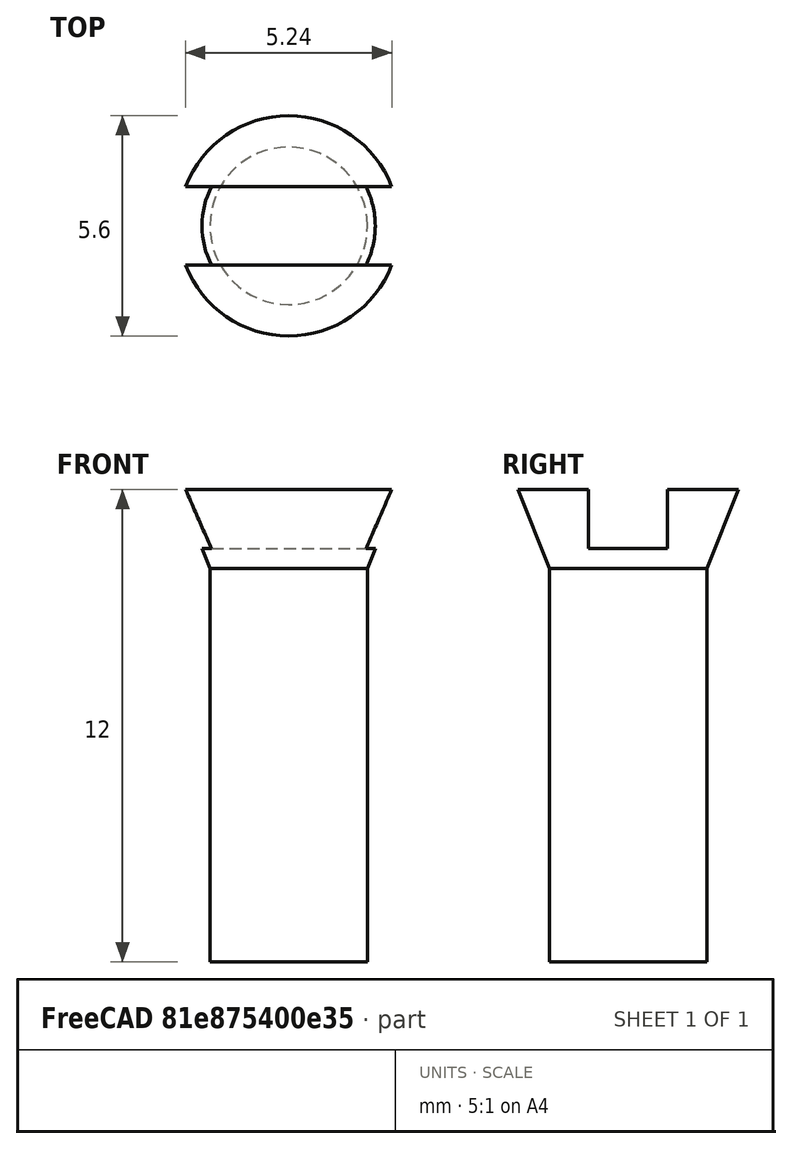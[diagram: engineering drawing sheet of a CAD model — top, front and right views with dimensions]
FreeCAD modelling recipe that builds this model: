
FCSTD DOCUMENT  (FreeCAD 0.21R33694 (Git))
Label: OJT1_T014R013_cargol
License: All rights reserved
LicenseURL: http://en.wikipedia.org/wiki/All_rights_reserved
objects: Part::Cylinder×1, Part::Cone×1, Part::Box×1, Part::MultiFuse×1, Part::Cut×1
note: 5 computed .brp shape members not serialized (recipe doc carries the construction recipe); baked Part::Feature solids carry a one-line shape summary decoded from their .brp

FEATURE [Part::Cylinder] Cylinder
  Angle = 360
  AttacherType = Attacher::AttachEngine3D
  FirstAngle = 0
  Height = 10
  Radius = 2
  SecondAngle = 0
FEATURE [Part::Cone] Cone
  Angle = 360
  AttacherType = Attacher::AttachEngine3D
  Height = 2
  Placement = pos=(0,0,10) rot=(0,0,1;0rad)
  Radius1 = 2
  Radius2 = 2.8
FEATURE [Part::Box] Box  label="Cube"
  AttacherType = Attacher::AttachEngine3D
  Height = 5
  Length = 9
  Placement = pos=(-4,-1,9.5) rot=(0,0,1;0rad)
  Width = 2
FEATURE [Part::MultiFuse] Fusion
  Refine = true
  Shapes = -> [Cone,Cylinder]
FEATURE [Part::Cut] Cut
  Base = -> Fusion
  Refine = true
  Tool = -> Box
